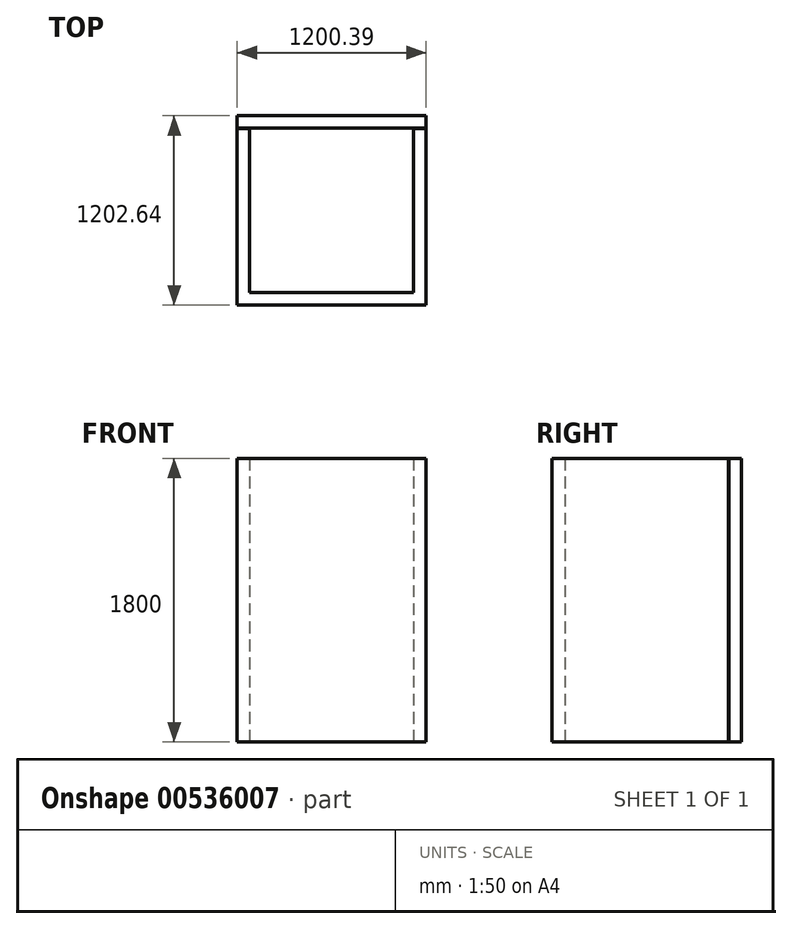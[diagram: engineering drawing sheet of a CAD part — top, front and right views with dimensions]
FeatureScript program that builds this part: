
annotation { "Feature Type Name" : "Feature", "Feature Type Description" : "" }
export const myFeature = defineFeature(function(context is Context, id is Id, definition is map)
    precondition{}
    {
        {
            var Q0;
            Q0=qCreatedBy(makeId("Top.planeOp"),FACE);
            var sketch = newSketch(context, id + "F0", { "sketchPlane" : qUnion([Q0])});
            skLineSegment(sketch, "E0.top", {"start": v(-1143.82, -49.38) * mm, "end": v(56.18, -49.38) * mm});
            skLineSegment(sketch, "E0.right", {"start": v(56.18, 1070.38) * mm, "end": v(56.18, -49.38) * mm});
            skLineSegment(sketch, "E1.0", {"start": v(-1063.82, 30.62) * mm, "end": v(-23.82, 30.62) * mm});
            skLineSegment(sketch, "E1.1", {"start": v(-1063.82, 1070.62) * mm, "end": v(-1063.82, 30.62) * mm});
            skLineSegment(sketch, "E2", {"start": v(-23.82, 1070.62) * mm, "end": v(-23.82, 30.62) * mm});
            skLineSegment(sketch, "E3", {"start": v(-1063.82, 1070.62) * mm, "end": v(-1143.82, 1070.62) * mm});
            skLineSegment(sketch, "E4", {"start": v(-1143.82, 1070.62) * mm, "end": v(-1143.82, -49.38) * mm});
            skLineSegment(sketch, "E5", {"start": v(56.18, 1070.38) * mm, "end": v(-23.82, 1070.62) * mm});
            skSolve(sketch);
        }
        {
            var Q0;
            Q0 = qSketchRegion(id + "F0", true);
            extrude(context, id + "F1", {"entities" : qUnion([Q0]), "depth" : 1800 * mm, "offsetDistance" : 25 * mm});
        }
        {
            var Q0;
            Q0=qCreatedBy(makeId("Top.planeOp"),FACE);
            var sketch = newSketch(context, id + "F2", { "sketchPlane" : qUnion([Q0])});
            skLineSegment(sketch, "E6", {"start": v(56.57, 1073.26) * mm, "end": v(56.57, 1153.26) * mm});
            skLineSegment(sketch, "E7", {"start": v(56.57, 1153.26) * mm, "end": v(-1143.43, 1153.26) * mm});
            skLineSegment(sketch, "E8", {"start": v(-1143.43, 1153.26) * mm, "end": v(-1143.43, 1073.26) * mm});
            skLineSegment(sketch, "E9", {"start": v(-1143.43, 1073.26) * mm, "end": v(56.57, 1073.26) * mm});
            skSolve(sketch);
        }
        {
            var Q0;
            Q0=makeQuery(id+"F2.imprint","IMPRINT",FACE,{"disambiguationData":[TD([[makeQuery(id+"F2.imprint","IMPRINT",EDGE,{"derivedFrom":sQuery(id+"F2.wireOp",EDGE,"E6")}),1.0]])]});
            extrude(context, id + "F3", {"entities" : qUnion([Q0]), "depth" : 1800 * mm, "offsetDistance" : 25 * mm});
        }
    });
